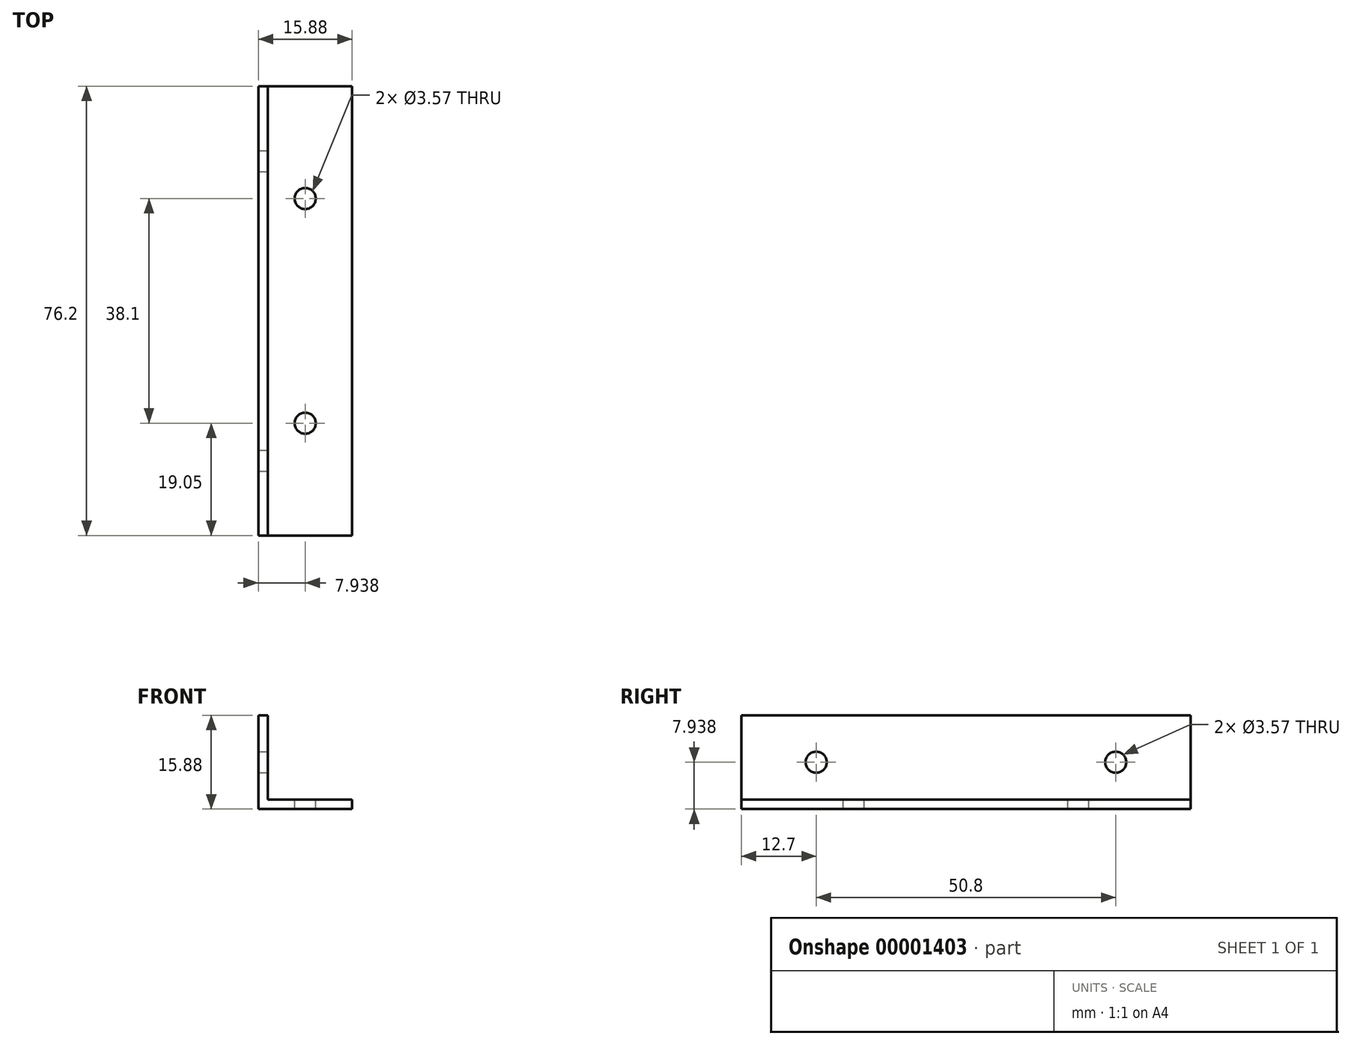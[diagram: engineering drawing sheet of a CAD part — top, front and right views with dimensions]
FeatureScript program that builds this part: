
annotation { "Feature Type Name" : "Feature", "Feature Type Description" : "" }
export const myFeature = defineFeature(function(context is Context, id is Id, definition is map)
    precondition{}
    {
        {
            var Q0;
            Q0=qCreatedBy(makeId("Front.planeOp"),FACE);
            var sketch = newSketch(context, id + "F0", { "sketchPlane" : qUnion([Q0])});
            skLineSegment(sketch, "E0", {"start": v(0, 0) * mm, "end": v(15.88, 0) * mm});
            skLineSegment(sketch, "E1", {"start": v(15.88, 0) * mm, "end": v(15.88, 1.59) * mm});
            skLineSegment(sketch, "E2", {"start": v(15.88, 1.59) * mm, "end": v(1.59, 1.59) * mm});
            skLineSegment(sketch, "E3", {"start": v(1.59, 1.59) * mm, "end": v(1.59, 15.88) * mm});
            skLineSegment(sketch, "E4", {"start": v(1.59, 15.88) * mm, "end": v(0, 15.88) * mm});
            skLineSegment(sketch, "E5", {"start": v(0, 15.88) * mm, "end": v(0, 0) * mm});
            skSolve(sketch);
        }
        {
            var Q0;
            Q0 = qSketchRegion(id + "F0", true);
            extrude(context, id + "F1", {"entities" : qUnion([Q0]), "endBound" : BoundingType.SYMMETRIC, "depth" : 76.2 * mm});
        }
        {
            var Q0;
            Q0=makeQuery(id+"F1.opExtrude","SWEPT_FACE",FACE,{"disambiguationData":[OSD([sQuery(id+"F0.wireOp",EDGE,"E3")])]});
            var sketch = newSketch(context, id + "F2", { "sketchPlane" : qUnion([Q0])});
            skCircle(sketch, "E6", {"center": v(-25.4, 7.94) * mm, "radius": 1.79 * mm});
            skCircle(sketch, "E7", {"center": v(25.4, 7.94) * mm, "radius": 1.79 * mm});
            skSolve(sketch);
        }
        {
            var Q0;
            Q0 = qSketchRegion(id + "F2", true);
            extrude(context, id + "F3", {"entities" : qUnion([Q0]), "operationType" : NewBodyOperationType.REMOVE, "endBound" : BoundingType.THROUGH_ALL, "oppositeDirection" : true, "depth" : 25.4 * mm});
        }
        {
            var Q0;
            Q0=makeQuery(id+"F1.opExtrude","SWEPT_FACE",FACE,{"disambiguationData":[OSD([sQuery(id+"F0.wireOp",EDGE,"E2")])]});
            var sketch = newSketch(context, id + "F4", { "sketchPlane" : qUnion([Q0])});
            skCircle(sketch, "E8", {"center": v(7.94, -19.05) * mm, "radius": 1.79 * mm});
            skCircle(sketch, "E9", {"center": v(7.94, 19.05) * mm, "radius": 1.79 * mm});
            skSolve(sketch);
        }
        {
            var Q0;
            Q0 = qSketchRegion(id + "F4", true);
            extrude(context, id + "F5", {"entities" : qUnion([Q0]), "operationType" : NewBodyOperationType.REMOVE, "endBound" : BoundingType.THROUGH_ALL, "oppositeDirection" : true, "depth" : 25.4 * mm});
        }
    });
